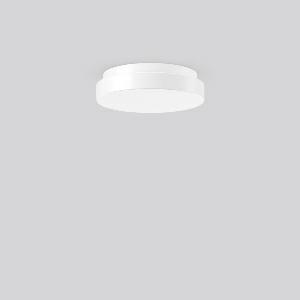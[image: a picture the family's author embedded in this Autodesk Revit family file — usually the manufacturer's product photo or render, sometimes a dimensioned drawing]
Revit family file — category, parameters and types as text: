
# Revit family: flat_kreis_211209_002_bcc6
name_source: partatom
category: Lighting Fixtures
units: mm (PartAtom-declared; Revit-internal decimal feet)

## family parameters
Cut with Voids When Loaded = No
Host = Face
Light Source = No
Part Type = Normal
Room Calculation Point = No
Round Connector Dimension = Use Diameter
Shared = No

## types (1)
- FLAT KREIS (1 x LED Modul 830, 1050 lm, 3000)
    Apparent Load = 12 VA
    CIE Flux Codes = 43 73 92 87 100
    Color Rendering = 80
    Color Temperature = 3000
    Default Elevation = 1800 mm
    Description = Series: FLAT KREIS
Decorative round surface-mounted luminaire. Base: plastic. Mouth blown 3-layer opal glass (Triplex glass) with satin finish. Diffuser fastening: spring system. Homogeneous and smooth light distribution. 
Colour: white
Diameter: 300 mm
Height: 75 mm
Lamp: LED exchangeable
Socket: without socket
Colour temperature: 3000K
Colour rendering index (CRI): 83
System power: 12 W
Rated luminous flux: 1050 lm
Beam angle Down: 120°
Luminous efficiency: 88 lm/W
Control gear: AC Strom, dim.Ph.an-/abschnitt
Protection class: I
Type of protection: IP 43
    Height = 75 mm
    Lamp = 1 x LED Modul 830
    Lamp Light Flux = 1050 lm
    Lamp count = 1
    Length = 300 mm
    Lifetime = 50000 h
    Luminous efficacy = 88 lm/W
    Manufacturer = RZB
    ModVariant = No
    Model = 211209.002
    Mounting Place = Ceiling, Wall
    Mounting Type = Surface mounted
    Number of Poles = 1
    OnlyDefault = Yes
    Power Factor = 1
    Product Name = FLAT KREIS
    Product group = Surface mounted ceiling and wall luminaires
    ProductGroupID = 305
    Protection Class = Protection class I
    Protection Degree = IP 43
    RLX_Detail_Level = 1
    RLX_Emergency_Light_Flux = 0 lm
    RLX_Emergency_Type = 0
    RLX_Emergency_Type_DB = No
    RlxData = <blob elided: 11169 chars, md5=76cb9304>
    Socket = socket
    Standby Power = 0 W
    System Light Flux = 1050 lm
    System Power = 12 W
    Type Comments = ALEA SPOT
    Type Image = 211209.912.79.jpg
    URL = http://relux.com
    VarID = ---
    Voltage = 230 V
    Voltage Range = 220-240 V
    Weight = 0.00 kg
    Width = 0 mm  [stored 0 ft]

note: [stored X ft] marks values corroborated as IEEE doubles in the binary element streams (Revit-internal decimal feet)

## geometry (parser evidence)
native form markers: Sweep x10
no freeform markers — native parametric forms only
